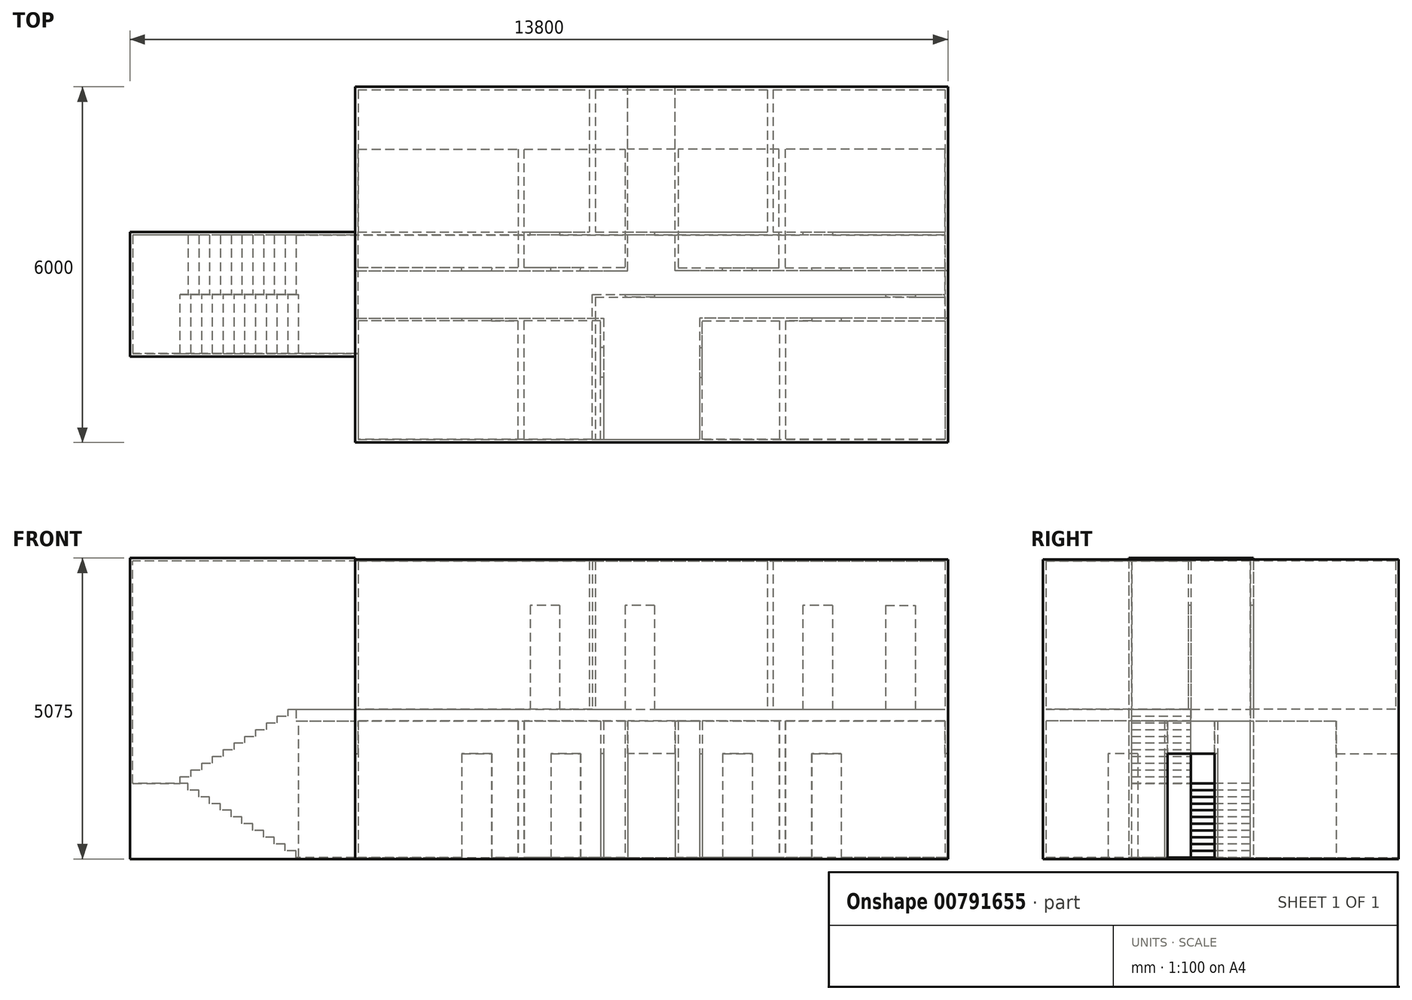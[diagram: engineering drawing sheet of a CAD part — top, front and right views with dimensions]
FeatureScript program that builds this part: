
annotation { "Feature Type Name" : "Feature", "Feature Type Description" : "" }
export const myFeature = defineFeature(function(context is Context, id is Id, definition is map)
    precondition{}
    {
        {
            var Q0;
            Q0=qCreatedBy(makeId("Top.planeOp"),FACE);
            var sketch = newSketch(context, id + "F0", { "sketchPlane" : qUnion([Q0])});
            skLineSegment(sketch, "E0.bottom", {"start": v(0, 0) * mm, "end": v(10000, 0) * mm});
            skLineSegment(sketch, "E0.top", {"start": v(0, 5000) * mm, "end": v(10000, 5000) * mm});
            skLineSegment(sketch, "E0.left", {"start": v(0, 0) * mm, "end": v(0, 5000) * mm});
            skLineSegment(sketch, "E0.right", {"start": v(10000, 0) * mm, "end": v(10000, 5000) * mm});
            skSolve(sketch);
        }
        {
            var Q0;
            Q0=qCreatedBy(makeId("Top.planeOp"),FACE);
            var sketch = newSketch(context, id + "F1", { "sketchPlane" : qUnion([Q0])});
            skLineSegment(sketch, "E1.bottom", {"start": v(0, 0) * mm, "end": v(5000, 0) * mm});
            skLineSegment(sketch, "E1.top", {"start": v(0, 5000) * mm, "end": v(4600, 5000) * mm});
            skLineSegment(sketch, "E1.left", {"start": v(0, 0) * mm, "end": v(0, 2100) * mm});
            skLineSegment(sketch, "E2", {"start": v(0, 2900) * mm, "end": v(1800, 2900) * mm});
            skLineSegment(sketch, "E3", {"start": v(0, 2100) * mm, "end": v(1800, 2100) * mm});
            skLineSegment(sketch, "E4", {"start": v(2800, 2900) * mm, "end": v(2800, 5000) * mm});
            skLineSegment(sketch, "E5", {"start": v(2792.35, 2100) * mm, "end": v(2792.35, 0) * mm});
            skLineSegment(sketch, "E6", {"start": v(2800, 2900) * mm, "end": v(3300, 2900) * mm});
            skLineSegment(sketch, "E7", {"start": v(4600, 2900) * mm, "end": v(4600, 5000) * mm});
            skLineSegment(sketch, "E8", {"start": v(2792.35, 2100) * mm, "end": v(4192.35, 2100) * mm});
            skLineSegment(sketch, "E9", {"start": v(4192.35, 2100) * mm, "end": v(4192.35, 1600) * mm});
            skPoint(sketch, "E10", {"position": v(1800, 2900) * mm});
            skPoint(sketch, "E11", {"position": v(2300, 2900) * mm});
            skPoint(sketch, "E12", {"position": v(1800, 2100) * mm});
            skPoint(sketch, "E13", {"position": v(2300, 2100) * mm});
            skPoint(sketch, "E14", {"position": v(4192.35, 1600) * mm});
            skPoint(sketch, "E15", {"position": v(3300, 2900) * mm});
            skPoint(sketch, "E16", {"position": v(3800, 2900) * mm});
            skPoint(sketch, "E17", {"position": v(4192.35, 1100) * mm});
            skLineSegment(sketch, "E18.trimOffspring", {"start": v(2300, 2900) * mm, "end": v(2800, 2900) * mm});
            skLineSegment(sketch, "E19.trimOffspring", {"start": v(2300, 2100) * mm, "end": v(2792.35, 2100) * mm});
            skLineSegment(sketch, "E20.trimOffspring", {"start": v(3800, 2900) * mm, "end": v(4600, 2900) * mm});
            skLineSegment(sketch, "E21.trimOffspring", {"start": v(4192.35, 1100) * mm, "end": v(4192.35, 0) * mm});
            skLineSegment(sketch, "E22.trimOffspring", {"start": v(0, 2900) * mm, "end": v(0, 5000) * mm});
            skLineSegment(sketch, "E23", {"start": v(1800, 2100) * mm, "end": v(1800, 2050) * mm});
            skLineSegment(sketch, "E24", {"start": v(1800, 2050) * mm, "end": v(50, 2050) * mm});
            skLineSegment(sketch, "E25", {"start": v(50, 2050) * mm, "end": v(50, 50) * mm});
            skLineSegment(sketch, "E26", {"start": v(50, 50) * mm, "end": v(2742.35, 50) * mm});
            skLineSegment(sketch, "E27", {"start": v(2300, 2100) * mm, "end": v(2300, 2050) * mm});
            skLineSegment(sketch, "E28", {"start": v(2300, 2050) * mm, "end": v(2742.35, 2050) * mm});
            skLineSegment(sketch, "E29", {"start": v(2742.35, 2050) * mm, "end": v(2742.35, 50) * mm});
            skLineSegment(sketch, "E30", {"start": v(4192.35, 1600) * mm, "end": v(4142.35, 1600) * mm});
            skLineSegment(sketch, "E31", {"start": v(4142.35, 1600) * mm, "end": v(4142.35, 2050) * mm});
            skLineSegment(sketch, "E32", {"start": v(4142.35, 2050) * mm, "end": v(2842.35, 2050) * mm});
            skLineSegment(sketch, "E33", {"start": v(2842.35, 2050) * mm, "end": v(2842.35, 50) * mm});
            skLineSegment(sketch, "E34", {"start": v(2842.35, 50) * mm, "end": v(4142.35, 50) * mm});
            skLineSegment(sketch, "E35", {"start": v(4192.35, 1100) * mm, "end": v(4142.35, 1100) * mm});
            skLineSegment(sketch, "E36", {"start": v(4142.35, 50) * mm, "end": v(4142.35, 1100) * mm});
            skLineSegment(sketch, "E37", {"start": v(4192.35, 50) * mm, "end": v(5000, 50) * mm});
            skLineSegment(sketch, "E38", {"start": v(5000, 0) * mm, "end": v(5000, 50) * mm});
            skLineSegment(sketch, "E39", {"start": v(1800, 2900) * mm, "end": v(1800, 2950) * mm});
            skLineSegment(sketch, "E40", {"start": v(1800, 2950) * mm, "end": v(50, 2950) * mm});
            skLineSegment(sketch, "E41", {"start": v(50, 2950) * mm, "end": v(50, 4950) * mm});
            skLineSegment(sketch, "E42", {"start": v(50, 4950) * mm, "end": v(2750, 4950) * mm});
            skLineSegment(sketch, "E43", {"start": v(2750, 4950) * mm, "end": v(2750, 2950) * mm});
            skLineSegment(sketch, "E44", {"start": v(2750, 2950) * mm, "end": v(2303.7, 2950) * mm});
            skLineSegment(sketch, "E45", {"start": v(2303.7, 2950) * mm, "end": v(2300, 2900) * mm});
            skLineSegment(sketch, "E46", {"start": v(3300, 2900) * mm, "end": v(3300, 2950) * mm});
            skLineSegment(sketch, "E47", {"start": v(3300, 2950) * mm, "end": v(2850, 2950) * mm});
            skLineSegment(sketch, "E48", {"start": v(2850, 2950) * mm, "end": v(2850, 4950) * mm});
            skLineSegment(sketch, "E49", {"start": v(2850, 4950) * mm, "end": v(4550, 4950) * mm});
            skLineSegment(sketch, "E50", {"start": v(4550, 4950) * mm, "end": v(4550, 2950) * mm});
            skLineSegment(sketch, "E51", {"start": v(4550, 2950) * mm, "end": v(3800.9, 2950) * mm});
            skLineSegment(sketch, "E52", {"start": v(3800, 2900) * mm, "end": v(3800.9, 2950) * mm});
            skSolve(sketch);
        }
        {
            var Q0;
            Q0 = qSketchRegion(id + "F0", true);
            extrude(context, id + "F2", {"entities" : qUnion([Q0]), "oppositeDirection" : true, "depth" : 25 * mm, "offsetDistance" : 25 * mm});
        }
        {
            var Q0;
            Q0 = qSketchRegion(id + "F1", true);
            extrude(context, id + "F3", {"entities" : qUnion([Q0]), "operationType" : NewBodyOperationType.ADD, "depth" : 2500 * mm, "offsetDistance" : 25 * mm});
        }
        {
            var Q0;
            Q0=qCreatedBy(makeId("Top.planeOp"),FACE);
            cPlane(context, id + "F4", {"entities" : qUnion([Q0]), "cplaneType" : CPlaneType.OFFSET, "offset" : 2500 * mm, "width" : 150 * mm, "height" : 150 * mm});
        }
        {
            var Q0;
            Q0=qCreatedBy(id+"F4.planeOp",FACE);
            var sketch = newSketch(context, id + "F5", { "sketchPlane" : qUnion([Q0])});
            skLineSegment(sketch, "E53.bottom", {"start": v(0, 0) * mm, "end": v(10000, 0) * mm});
            skLineSegment(sketch, "E53.top", {"start": v(0, 5000) * mm, "end": v(10000, 5000) * mm});
            skLineSegment(sketch, "E53.left", {"start": v(0, 0) * mm, "end": v(0, 5000) * mm});
            skLineSegment(sketch, "E53.right", {"start": v(10000, 0) * mm, "end": v(10000, 5000) * mm});
            skSolve(sketch);
        }
        {
            var Q0;
            Q0 = qSketchRegion(id + "F5", true);
            extrude(context, id + "F6", {"entities" : qUnion([Q0]), "operationType" : NewBodyOperationType.ADD, "oppositeDirection" : true, "depth" : 200 * mm, "offsetDistance" : 25 * mm});
        }
        {
            var Q0;
            Q0=qCreatedBy(id+"F4.planeOp",FACE);
            var sketch = newSketch(context, id + "F7", { "sketchPlane" : qUnion([Q0])});
            skLineSegment(sketch, "E54.bottom", {"start": v(0, 0) * mm, "end": v(5000, 0) * mm});
            skLineSegment(sketch, "E54.top", {"start": v(0, 5000) * mm, "end": v(4600, 5000) * mm});
            skLineSegment(sketch, "E54.left", {"start": v(0, 0) * mm, "end": v(0, 2100) * mm});
            skLineSegment(sketch, "E55", {"start": v(0, 2900) * mm, "end": v(1800, 2900) * mm});
            skLineSegment(sketch, "E56", {"start": v(0, 2100) * mm, "end": v(1800, 2100) * mm});
            skLineSegment(sketch, "E57", {"start": v(2800, 2900) * mm, "end": v(2800, 5000) * mm});
            skLineSegment(sketch, "E58", {"start": v(2792.35, 2100) * mm, "end": v(2792.35, 0) * mm});
            skLineSegment(sketch, "E59", {"start": v(2800, 2900) * mm, "end": v(3300, 2900) * mm});
            skLineSegment(sketch, "E60", {"start": v(4600, 2900) * mm, "end": v(4600, 5000) * mm});
            skLineSegment(sketch, "E61", {"start": v(2792.35, 2100) * mm, "end": v(4192.35, 2100) * mm});
            skLineSegment(sketch, "E62", {"start": v(4192.35, 2100) * mm, "end": v(4192.35, 1600) * mm});
            skPoint(sketch, "E63", {"position": v(1800, 2900) * mm});
            skPoint(sketch, "E64", {"position": v(2300, 2900) * mm});
            skPoint(sketch, "E65", {"position": v(1800, 2100) * mm});
            skPoint(sketch, "E66", {"position": v(2300, 2100) * mm});
            skPoint(sketch, "E67", {"position": v(4192.35, 1600) * mm});
            skPoint(sketch, "E68", {"position": v(3300, 2900) * mm});
            skPoint(sketch, "E69", {"position": v(3800, 2900) * mm});
            skPoint(sketch, "E70", {"position": v(4192.35, 1100) * mm});
            skLineSegment(sketch, "E71.trimOffspring", {"start": v(2300, 2900) * mm, "end": v(2800, 2900) * mm});
            skLineSegment(sketch, "E72.trimOffspring", {"start": v(2300, 2100) * mm, "end": v(2792.35, 2100) * mm});
            skLineSegment(sketch, "E73.trimOffspring", {"start": v(3800, 2900) * mm, "end": v(4600, 2900) * mm});
            skLineSegment(sketch, "E74.trimOffspring", {"start": v(4192.35, 1100) * mm, "end": v(4192.35, 0) * mm});
            skLineSegment(sketch, "E75.trimOffspring", {"start": v(0, 2900) * mm, "end": v(0, 5000) * mm});
            skLineSegment(sketch, "E76", {"start": v(1800, 2100) * mm, "end": v(1800, 2050) * mm});
            skLineSegment(sketch, "E77", {"start": v(1800, 2050) * mm, "end": v(50, 2050) * mm});
            skLineSegment(sketch, "E78", {"start": v(50, 2050) * mm, "end": v(50, 50) * mm});
            skLineSegment(sketch, "E79", {"start": v(50, 50) * mm, "end": v(2742.35, 50) * mm});
            skLineSegment(sketch, "E80", {"start": v(2300, 2100) * mm, "end": v(2300, 2050) * mm});
            skLineSegment(sketch, "E81", {"start": v(2300, 2050) * mm, "end": v(2742.35, 2050) * mm});
            skLineSegment(sketch, "E82", {"start": v(2742.35, 2050) * mm, "end": v(2742.35, 50) * mm});
            skLineSegment(sketch, "E83", {"start": v(4192.35, 1600) * mm, "end": v(4142.35, 1600) * mm});
            skLineSegment(sketch, "E84", {"start": v(4142.35, 1600) * mm, "end": v(4142.35, 2050) * mm});
            skLineSegment(sketch, "E85", {"start": v(4142.35, 2050) * mm, "end": v(2842.35, 2050) * mm});
            skLineSegment(sketch, "E86", {"start": v(2842.35, 2050) * mm, "end": v(2842.35, 50) * mm});
            skLineSegment(sketch, "E87", {"start": v(2842.35, 50) * mm, "end": v(4142.35, 50) * mm});
            skLineSegment(sketch, "E88", {"start": v(4192.35, 1100) * mm, "end": v(4142.35, 1100) * mm});
            skLineSegment(sketch, "E89", {"start": v(4142.35, 50) * mm, "end": v(4142.35, 1100) * mm});
            skLineSegment(sketch, "E90", {"start": v(4192.35, 50) * mm, "end": v(5000, 50) * mm});
            skLineSegment(sketch, "E91", {"start": v(5000, 0) * mm, "end": v(5000, 50) * mm});
            skLineSegment(sketch, "E92", {"start": v(1800, 2900) * mm, "end": v(1800, 2950) * mm});
            skLineSegment(sketch, "E93", {"start": v(1800, 2950) * mm, "end": v(50, 2950) * mm});
            skLineSegment(sketch, "E94", {"start": v(50, 2950) * mm, "end": v(50, 4950) * mm});
            skLineSegment(sketch, "E95", {"start": v(50, 4950) * mm, "end": v(2750, 4950) * mm});
            skLineSegment(sketch, "E96", {"start": v(2750, 4950) * mm, "end": v(2750, 2950) * mm});
            skLineSegment(sketch, "E97", {"start": v(2750, 2950) * mm, "end": v(2303.7, 2950) * mm});
            skLineSegment(sketch, "E98", {"start": v(2303.7, 2950) * mm, "end": v(2300, 2900) * mm});
            skLineSegment(sketch, "E99", {"start": v(3300, 2900) * mm, "end": v(3300, 2950) * mm});
            skLineSegment(sketch, "E100", {"start": v(3300, 2950) * mm, "end": v(2850, 2950) * mm});
            skLineSegment(sketch, "E101", {"start": v(2850, 2950) * mm, "end": v(2850, 4950) * mm});
            skLineSegment(sketch, "E102", {"start": v(2850, 4950) * mm, "end": v(4550, 4950) * mm});
            skLineSegment(sketch, "E103", {"start": v(4550, 4950) * mm, "end": v(4550, 2950) * mm});
            skLineSegment(sketch, "E104", {"start": v(4550, 2950) * mm, "end": v(3800.9, 2950) * mm});
            skLineSegment(sketch, "E105", {"start": v(3800, 2900) * mm, "end": v(3800.9, 2950) * mm});
            skLineSegment(sketch, "E106", {"start": v(0, 2900) * mm, "end": v(0, 2100) * mm});
            skLineSegment(sketch, "E107", {"start": v(50, 2050) * mm, "end": v(50, 2950) * mm});
            skLineSegment(sketch, "E108", {"start": v(1800, 2050) * mm, "end": v(2300, 2050) * mm});
            skLineSegment(sketch, "E109", {"start": v(2300, 2100) * mm, "end": v(1800, 2100) * mm});
            skLineSegment(sketch, "E110", {"start": v(1800, 2900) * mm, "end": v(2300, 2900) * mm});
            skLineSegment(sketch, "E111", {"start": v(1800, 2950) * mm, "end": v(2303.7, 2950) * mm});
            skLineSegment(sketch, "E112", {"start": v(3300, 2900) * mm, "end": v(3800, 2900) * mm});
            skLineSegment(sketch, "E113", {"start": v(3800.9, 2950) * mm, "end": v(3300, 2950) * mm});
            skLineSegment(sketch, "E114", {"start": v(4192.35, 1600) * mm, "end": v(4192.35, 1100) * mm});
            skLineSegment(sketch, "E115", {"start": v(4142.35, 1100) * mm, "end": v(4142.35, 1600) * mm});
            skLineSegment(sketch, "E116", {"start": v(4600, 5000) * mm, "end": v(5000, 5000) * mm});
            skLineSegment(sketch, "E117", {"start": v(5000, 5000) * mm, "end": v(5000, 4950) * mm});
            skLineSegment(sketch, "E118", {"start": v(5000, 4950) * mm, "end": v(4550, 4950) * mm});
            skSolve(sketch);
        }
        {
            var Q0;
            Q0 = qSketchRegion(id + "F7", true);
            extrude(context, id + "F8", {"entities" : qUnion([Q0]), "operationType" : NewBodyOperationType.ADD, "oppositeDirection" : true, "depth" : 750 * mm, "offsetDistance" : 25 * mm});
        }
        {
            var Q0;
            Q0=makeQuery(id+"F2.opExtrude","SWEPT_BODY",BODY,{"disambiguationData":[OSD([sQuery(id+"F0.wireOp",EDGE,"E0.bottom"),sQuery(id+"F0.wireOp",EDGE,"E0.top"),sQuery(id+"F0.wireOp",EDGE,"E0.left"),sQuery(id+"F0.wireOp",EDGE,"E0.right")])]});
            var Q1;
            Q1=makeQuery(id+"F3.opExtrude","SWEPT_FACE",FACE,{"disambiguationData":[OSD([sQuery(id+"F1.wireOp",EDGE,"E38")])]});
            mirror(context, id + "F9", {"operationType" : NewBodyOperationType.ADD, "entities" : qUnion([Q0]), "mirrorPlane" : qUnion([Q1])});
        }
        {
            var Q0;
            Q0=qCreatedBy(makeId("Front.planeOp"),FACE);
            cPlane(context, id + "F10", {"entities" : qUnion([Q0]), "cplaneType" : CPlaneType.OFFSET, "offset" : 2500 * mm, "oppositeDirection" : true, "width" : 150 * mm, "height" : 150 * mm});
        }
        {
            var Q0;
            Q0=qCreatedBy(id+"F10.planeOp",FACE);
            var sketch = newSketch(context, id + "F11", { "sketchPlane" : qUnion([Q0])});
            skLineSegment(sketch, "E119.bottom", {"start": v(-1000, 0) * mm, "end": v(-3000, 0) * mm});
            skLineSegment(sketch, "E119.right", {"start": v(-3000, 0) * mm, "end": v(-3000, 1250) * mm});
            skLineSegment(sketch, "E120", {"start": v(-1000, 0) * mm, "end": v(-3000, 1250) * mm});
            skLineSegment(sketch, "E121.bottom", {"start": v(-1000, 0) * mm, "end": v(-1181.82, 0) * mm});
            skLineSegment(sketch, "E121.top", {"start": v(-1000, 113.64) * mm, "end": v(-1181.82, 113.64) * mm});
            skLineSegment(sketch, "E121.left", {"start": v(-1000, 0) * mm, "end": v(-1000, 113.64) * mm});
            skLineSegment(sketch, "E121.right", {"start": v(-1181.82, 0) * mm, "end": v(-1181.82, 113.64) * mm});
            skLineSegment(sketch, "E122.bottom", {"start": v(-1181.82, 0) * mm, "end": v(-1363.64, 0) * mm});
            skLineSegment(sketch, "E122.top", {"start": v(-1181.82, 227.27) * mm, "end": v(-1363.64, 227.27) * mm});
            skLineSegment(sketch, "E122.left", {"start": v(-1181.82, 0) * mm, "end": v(-1181.82, 227.27) * mm});
            skLineSegment(sketch, "E122.right", {"start": v(-1363.64, 0) * mm, "end": v(-1363.64, 227.27) * mm});
            skLineSegment(sketch, "E123.bottom", {"start": v(-1363.64, 0) * mm, "end": v(-1545.45, 0) * mm});
            skLineSegment(sketch, "E123.top", {"start": v(-1363.64, 340.9) * mm, "end": v(-1545.45, 340.9) * mm});
            skLineSegment(sketch, "E123.left", {"start": v(-1363.64, 0) * mm, "end": v(-1363.64, 340.9) * mm});
            skLineSegment(sketch, "E123.right", {"start": v(-1545.45, 0) * mm, "end": v(-1545.45, 340.9) * mm});
            skLineSegment(sketch, "E124.bottom", {"start": v(-1545.45, 0) * mm, "end": v(-1727.27, 0) * mm});
            skLineSegment(sketch, "E124.top", {"start": v(-1545.45, 454.55) * mm, "end": v(-1727.27, 454.55) * mm});
            skLineSegment(sketch, "E124.left", {"start": v(-1545.45, 0) * mm, "end": v(-1545.45, 454.55) * mm});
            skLineSegment(sketch, "E124.right", {"start": v(-1727.27, 0) * mm, "end": v(-1727.27, 454.55) * mm});
            skLineSegment(sketch, "E125.bottom", {"start": v(-1727.27, 0) * mm, "end": v(-1909.1, 0) * mm});
            skLineSegment(sketch, "E125.top", {"start": v(-1727.27, 568.18) * mm, "end": v(-1909.1, 568.18) * mm});
            skLineSegment(sketch, "E125.left", {"start": v(-1727.27, 0) * mm, "end": v(-1727.27, 568.18) * mm});
            skLineSegment(sketch, "E125.right", {"start": v(-1909.1, 0) * mm, "end": v(-1909.1, 568.18) * mm});
            skLineSegment(sketch, "E126.bottom", {"start": v(-1909.1, 0) * mm, "end": v(-2090.9, 0) * mm});
            skLineSegment(sketch, "E126.top", {"start": v(-1909.1, 681.81) * mm, "end": v(-2090.9, 681.81) * mm});
            skLineSegment(sketch, "E126.left", {"start": v(-1909.1, 0) * mm, "end": v(-1909.1, 681.81) * mm});
            skLineSegment(sketch, "E126.right", {"start": v(-2090.9, 0) * mm, "end": v(-2090.9, 681.81) * mm});
            skLineSegment(sketch, "E127.bottom", {"start": v(-2090.9, 0) * mm, "end": v(-2272.72, 0) * mm});
            skLineSegment(sketch, "E127.top", {"start": v(-2090.9, 795.45) * mm, "end": v(-2272.72, 795.45) * mm});
            skLineSegment(sketch, "E127.left", {"start": v(-2090.9, 0) * mm, "end": v(-2090.9, 795.45) * mm});
            skLineSegment(sketch, "E127.right", {"start": v(-2272.72, 0) * mm, "end": v(-2272.72, 795.45) * mm});
            skLineSegment(sketch, "E128.bottom", {"start": v(-2272.72, 0) * mm, "end": v(-2454.54, 0) * mm});
            skLineSegment(sketch, "E128.top", {"start": v(-2272.72, 909.09) * mm, "end": v(-2454.54, 909.09) * mm});
            skLineSegment(sketch, "E128.left", {"start": v(-2272.72, 0) * mm, "end": v(-2272.72, 909.09) * mm});
            skLineSegment(sketch, "E128.right", {"start": v(-2454.54, 0) * mm, "end": v(-2454.54, 909.09) * mm});
            skLineSegment(sketch, "E129.bottom", {"start": v(-2454.54, 0) * mm, "end": v(-2636.36, 0) * mm});
            skLineSegment(sketch, "E129.top", {"start": v(-2454.54, 1022.72) * mm, "end": v(-2636.36, 1022.72) * mm});
            skLineSegment(sketch, "E129.left", {"start": v(-2454.54, 0) * mm, "end": v(-2454.54, 1022.72) * mm});
            skLineSegment(sketch, "E129.right", {"start": v(-2636.36, 0) * mm, "end": v(-2636.36, 1022.72) * mm});
            skLineSegment(sketch, "E130.bottom", {"start": v(-2636.36, 0) * mm, "end": v(-2818.17, 0) * mm});
            skLineSegment(sketch, "E130.top", {"start": v(-2636.36, 1136.36) * mm, "end": v(-2818.17, 1136.36) * mm});
            skLineSegment(sketch, "E130.left", {"start": v(-2636.36, 0) * mm, "end": v(-2636.36, 1136.36) * mm});
            skLineSegment(sketch, "E130.right", {"start": v(-2818.17, 0) * mm, "end": v(-2818.17, 1136.36) * mm});
            skLineSegment(sketch, "E131.bottom", {"start": v(-3000, 0) * mm, "end": v(-3750, 0) * mm});
            skLineSegment(sketch, "E131.top", {"start": v(-3000, 1250) * mm, "end": v(-3750, 1250) * mm});
            skLineSegment(sketch, "E131.right", {"start": v(-3750, 0) * mm, "end": v(-3750, 1250) * mm});
            skLineSegment(sketch, "E132.bottom", {"start": v(-2818.17, 0) * mm, "end": v(-3000, 0) * mm});
            skLineSegment(sketch, "E132.top", {"start": v(-2818.17, 1250) * mm, "end": v(-3000, 1250) * mm});
            skLineSegment(sketch, "E132.left", {"start": v(-2818.17, 0) * mm, "end": v(-2818.17, 1250) * mm});
            skSolve(sketch);
        }
        {
            var Q0;
            Q0 = qSketchRegion(id + "F11", true);
            var Q1;
            {var subQ0=makeQuery(id+"F8.boolean.opBoolean","MERGE",FACE,{"derivedFrom":[makeQuery(id+"F6.boolean.opBoolean","MERGE",FACE,{"derivedFrom":[makeQuery(id+"F3.boolean.opBoolean","MERGE",FACE,{"derivedFrom":[makeQuery(id+"F2.opExtrude","SWEPT_FACE",FACE,{"disambiguationData":[OSD([sQuery(id+"F0.wireOp",EDGE,"E0.top")])]}),makeQuery(id+"F3.opExtrude","SWEPT_FACE",FACE,{"disambiguationData":[OSD([sQuery(id+"F1.wireOp",EDGE,"E1.top")])]})]}),makeQuery(id+"F6.opExtrude","SWEPT_FACE",FACE,{"disambiguationData":[OSD([sQuery(id+"F5.wireOp",EDGE,"E53.top")])]})]}),makeQuery(id+"F8.opExtrude","SWEPT_FACE",FACE,{"disambiguationData":[OSD([sQuery(id+"F7.wireOp",EDGE,"E54.top"),sQuery(id+"F7.wireOp",EDGE,"E116")])]})]});Q1=makeQuery(id+"F9.boolean.opBoolean","MERGE",FACE,{"derivedFrom":[subQ0,makeQuery(id+"F9.opPattern","COPY",FACE,{"derivedFrom":subQ0,"instanceName":"1"})]});}
            extrude(context, id + "F12", {"entities" : qUnion([Q0, Q1]), "operationType" : NewBodyOperationType.ADD, "oppositeDirection" : true, "depth" : 1000 * mm, "offsetDistance" : 25 * mm});
        }
        {
            var Q0;
            Q0=qCreatedBy(id+"F10.planeOp",FACE);
            var sketch = newSketch(context, id + "F13", { "sketchPlane" : qUnion([Q0])});
            skLineSegment(sketch, "E133.bottom", {"start": v(-3750, 0) * mm, "end": v(-2950, 0) * mm});
            skLineSegment(sketch, "E133.top", {"start": v(-3750, 1250) * mm, "end": v(-2950, 1250) * mm});
            skLineSegment(sketch, "E133.left", {"start": v(-3750, 0) * mm, "end": v(-3750, 1250) * mm});
            skLineSegment(sketch, "E133.right", {"start": v(-2950, 0) * mm, "end": v(-2950, 1250) * mm});
            skLineSegment(sketch, "E134", {"start": v(-2950, 1250) * mm, "end": v(-950, 1250) * mm});
            skLineSegment(sketch, "E135", {"start": v(-2950, 0) * mm, "end": v(-950, 0) * mm});
            skLineSegment(sketch, "E136", {"start": v(-950, 0) * mm, "end": v(-950, 1250) * mm});
            skLineSegment(sketch, "E137", {"start": v(-950, 1250) * mm, "end": v(-950, 2500) * mm});
            skLineSegment(sketch, "E138", {"start": v(-2950, 1250) * mm, "end": v(-950, 2500) * mm});
            skLineSegment(sketch, "E139.bottom", {"start": v(-2950, 1250) * mm, "end": v(-2768.18, 1250) * mm});
            skLineSegment(sketch, "E139.top", {"start": v(-2950, 1363.64) * mm, "end": v(-2768.18, 1363.64) * mm});
            skLineSegment(sketch, "E139.left", {"start": v(-2950, 1250) * mm, "end": v(-2950, 1363.64) * mm});
            skLineSegment(sketch, "E139.right", {"start": v(-2768.18, 1250) * mm, "end": v(-2768.18, 1363.64) * mm});
            skLineSegment(sketch, "E140.bottom", {"start": v(-2768.18, 1250) * mm, "end": v(-2586.36, 1250) * mm});
            skLineSegment(sketch, "E140.top", {"start": v(-2768.18, 1477.27) * mm, "end": v(-2586.36, 1477.27) * mm});
            skLineSegment(sketch, "E140.left", {"start": v(-2768.18, 1250) * mm, "end": v(-2768.18, 1477.27) * mm});
            skLineSegment(sketch, "E140.right", {"start": v(-2586.36, 1250) * mm, "end": v(-2586.36, 1477.27) * mm});
            skLineSegment(sketch, "E141.bottom", {"start": v(-2586.36, 1250) * mm, "end": v(-2404.55, 1250) * mm});
            skLineSegment(sketch, "E141.top", {"start": v(-2586.36, 1590.9) * mm, "end": v(-2404.55, 1590.9) * mm});
            skLineSegment(sketch, "E141.left", {"start": v(-2586.36, 1250) * mm, "end": v(-2586.36, 1590.9) * mm});
            skLineSegment(sketch, "E141.right", {"start": v(-2404.55, 1250) * mm, "end": v(-2404.55, 1590.9) * mm});
            skLineSegment(sketch, "E142.bottom", {"start": v(-2404.55, 1250) * mm, "end": v(-2222.74, 1250) * mm});
            skLineSegment(sketch, "E142.top", {"start": v(-2404.55, 1704.54) * mm, "end": v(-2222.74, 1704.54) * mm});
            skLineSegment(sketch, "E142.left", {"start": v(-2404.55, 1250) * mm, "end": v(-2404.55, 1704.54) * mm});
            skLineSegment(sketch, "E142.right", {"start": v(-2222.74, 1250) * mm, "end": v(-2222.74, 1704.54) * mm});
            skLineSegment(sketch, "E143.bottom", {"start": v(-2222.74, 1250) * mm, "end": v(-2040.92, 1250) * mm});
            skLineSegment(sketch, "E143.top", {"start": v(-2222.74, 1818.18) * mm, "end": v(-2040.92, 1818.18) * mm});
            skLineSegment(sketch, "E143.left", {"start": v(-2222.74, 1250) * mm, "end": v(-2222.74, 1818.18) * mm});
            skLineSegment(sketch, "E143.right", {"start": v(-2040.92, 1250) * mm, "end": v(-2040.92, 1818.18) * mm});
            skLineSegment(sketch, "E144.bottom", {"start": v(-2040.92, 1250) * mm, "end": v(-1859.1, 1250) * mm});
            skLineSegment(sketch, "E144.top", {"start": v(-2040.92, 1931.81) * mm, "end": v(-1859.1, 1931.81) * mm});
            skLineSegment(sketch, "E144.left", {"start": v(-2040.92, 1250) * mm, "end": v(-2040.92, 1931.81) * mm});
            skLineSegment(sketch, "E144.right", {"start": v(-1859.1, 1250) * mm, "end": v(-1859.1, 1931.81) * mm});
            skLineSegment(sketch, "E145.bottom", {"start": v(-1859.1, 1250) * mm, "end": v(-1677.29, 1250) * mm});
            skLineSegment(sketch, "E145.top", {"start": v(-1859.1, 2045.44) * mm, "end": v(-1677.29, 2045.44) * mm});
            skLineSegment(sketch, "E145.left", {"start": v(-1859.1, 1250) * mm, "end": v(-1859.1, 2045.44) * mm});
            skLineSegment(sketch, "E145.right", {"start": v(-1677.29, 1250) * mm, "end": v(-1677.29, 2045.44) * mm});
            skLineSegment(sketch, "E146.bottom", {"start": v(-1677.29, 1250) * mm, "end": v(-1495.47, 1250) * mm});
            skLineSegment(sketch, "E146.top", {"start": v(-1677.29, 2159.08) * mm, "end": v(-1495.47, 2159.08) * mm});
            skLineSegment(sketch, "E146.left", {"start": v(-1677.29, 1250) * mm, "end": v(-1677.29, 2159.08) * mm});
            skLineSegment(sketch, "E146.right", {"start": v(-1495.47, 1250) * mm, "end": v(-1495.47, 2159.08) * mm});
            skLineSegment(sketch, "E147.bottom", {"start": v(-1495.47, 1250) * mm, "end": v(-1313.65, 1250) * mm});
            skLineSegment(sketch, "E147.top", {"start": v(-1495.47, 2272.72) * mm, "end": v(-1313.65, 2272.72) * mm});
            skLineSegment(sketch, "E147.left", {"start": v(-1495.47, 1250) * mm, "end": v(-1495.47, 2272.72) * mm});
            skLineSegment(sketch, "E147.right", {"start": v(-1313.65, 1250) * mm, "end": v(-1313.65, 2272.72) * mm});
            skLineSegment(sketch, "E148.bottom", {"start": v(-1313.65, 1250) * mm, "end": v(-1131.84, 1250) * mm});
            skLineSegment(sketch, "E148.top", {"start": v(-1313.65, 2386.35) * mm, "end": v(-1131.84, 2386.35) * mm});
            skLineSegment(sketch, "E148.left", {"start": v(-1313.65, 1250) * mm, "end": v(-1313.65, 2386.35) * mm});
            skLineSegment(sketch, "E148.right", {"start": v(-1131.84, 1250) * mm, "end": v(-1131.84, 2386.35) * mm});
            skLineSegment(sketch, "E149.bottom", {"start": v(-1131.84, 1250) * mm, "end": v(-950, 1250) * mm});
            skLineSegment(sketch, "E149.top", {"start": v(-1131.84, 2500) * mm, "end": v(-950, 2500) * mm});
            skLineSegment(sketch, "E149.left", {"start": v(-1131.84, 1250) * mm, "end": v(-1131.84, 2500) * mm});
            skSolve(sketch);
        }
        {
            var Q0;
            Q0 = qSketchRegion(id + "F13", true);
            extrude(context, id + "F14", {"entities" : qUnion([Q0]), "operationType" : NewBodyOperationType.ADD, "depth" : 1000 * mm, "offsetDistance" : 25 * mm});
        }
        {
            var Q0;
            Q0=makeQuery(id+"F8.boolean.opBoolean","MERGE",FACE,{"derivedFrom":[makeQuery(id+"F6.boolean.opBoolean","MERGE",FACE,{"derivedFrom":[makeQuery(id+"F3.boolean.opBoolean","MERGE",FACE,{"derivedFrom":[makeQuery(id+"F2.opExtrude","SWEPT_FACE",FACE,{"disambiguationData":[OSD([sQuery(id+"F0.wireOp",EDGE,"E0.left")])]}),makeQuery(id+"F3.opExtrude","SWEPT_FACE",FACE,{"disambiguationData":[OSD([sQuery(id+"F1.wireOp",EDGE,"E1.left")])]}),makeQuery(id+"F3.opExtrude","SWEPT_FACE",FACE,{"disambiguationData":[OSD([sQuery(id+"F1.wireOp",EDGE,"E22.trimOffspring")])]})]}),makeQuery(id+"F6.opExtrude","SWEPT_FACE",FACE,{"disambiguationData":[OSD([sQuery(id+"F5.wireOp",EDGE,"E53.left")])]})]}),makeQuery(id+"F8.opExtrude","SWEPT_FACE",FACE,{"disambiguationData":[OSD([sQuery(id+"F7.wireOp",EDGE,"E54.left"),sQuery(id+"F7.wireOp",EDGE,"E75.trimOffspring"),sQuery(id+"F7.wireOp",EDGE,"E106")])]})]});
            var sketch = newSketch(context, id + "F15", { "sketchPlane" : qUnion([Q0])});
            skLineSegment(sketch, "E150.top", {"start": v(-1500, 2500) * mm, "end": v(-3500, 2500) * mm});
            skLineSegment(sketch, "E151", {"start": v(-3500, 2500) * mm, "end": v(-3500, 2300) * mm});
            skLineSegment(sketch, "E152", {"start": v(-1500, 2500) * mm, "end": v(-1500, 2300) * mm});
            skLineSegment(sketch, "E153", {"start": v(-1500, 2300) * mm, "end": v(-3500, 2300) * mm});
            skSolve(sketch);
        }
        {
            var Q0;
            Q0 = qSketchRegion(id + "F15", true);
            extrude(context, id + "F16", {"entities" : qUnion([Q0]), "operationType" : NewBodyOperationType.ADD, "depth" : 1000 * mm, "offsetDistance" : 25 * mm});
        }
        {
            var Q0;
            Q0=makeQuery(id+"F14.boolean.opBoolean","MERGE",FACE,{"derivedFrom":[makeQuery(id+"F12.opExtrude","SWEPT_FACE",FACE,{"disambiguationData":[OSD([sQuery(id+"F11.wireOp",EDGE,"E131.right")])]}),makeQuery(id+"F14.opExtrude","SWEPT_FACE",FACE,{"disambiguationData":[OSD([sQuery(id+"F13.wireOp",EDGE,"E133.left")])]})]});
            var sketch = newSketch(context, id + "F17", { "sketchPlane" : qUnion([Q0])});
            skLineSegment(sketch, "E154.bottom", {"start": v(-3500, 0) * mm, "end": v(-1500, 0) * mm});
            skLineSegment(sketch, "E154.top", {"start": v(-3500, 5000) * mm, "end": v(-1500, 5000) * mm});
            skLineSegment(sketch, "E154.left", {"start": v(-3500, 0) * mm, "end": v(-3500, 5000) * mm});
            skLineSegment(sketch, "E154.right", {"start": v(-1500, 0) * mm, "end": v(-1500, 5000) * mm});
            skLineSegment(sketch, "E155.bottom", {"start": v(-3550, 5050) * mm, "end": v(-1450, 5050) * mm});
            skLineSegment(sketch, "E155.top", {"start": v(-3550, -25) * mm, "end": v(-1450, -25) * mm});
            skLineSegment(sketch, "E155.left", {"start": v(-3550, 5050) * mm, "end": v(-3550, -25) * mm});
            skLineSegment(sketch, "E155.right", {"start": v(-1450, 5050) * mm, "end": v(-1450, -25) * mm});
            skSolve(sketch);
        }
        {
            var Q0;
            Q0 = qSketchRegion(id + "F17", true);
            extrude(context, id + "F18", {"entities" : qUnion([Q0]), "operationType" : NewBodyOperationType.ADD, "oppositeDirection" : true, "depth" : 3750 * mm, "offsetDistance" : 25 * mm});
        }
        {
            var Q0;
            Q0=makeQuery(id+"F18.boolean.opBoolean","MERGE",FACE,{"derivedFrom":[makeQuery(id+"F14.boolean.opBoolean","MERGE",FACE,{"derivedFrom":[makeQuery(id+"F12.opExtrude","SWEPT_FACE",FACE,{"disambiguationData":[OSD([sQuery(id+"F11.wireOp",EDGE,"E131.right")])]}),makeQuery(id+"F14.opExtrude","SWEPT_FACE",FACE,{"disambiguationData":[OSD([sQuery(id+"F13.wireOp",EDGE,"E133.left")])]})]}),makeQuery(id+"F18.opExtrude","CAP_FACE",FACE,{"disambiguationData":[OSD([sQuery(id+"F17.wireOp",EDGE,"E154.bottom"),sQuery(id+"F17.wireOp",EDGE,"E154.top"),sQuery(id+"F17.wireOp",EDGE,"E154.left"),sQuery(id+"F17.wireOp",EDGE,"E154.right"),sQuery(id+"F17.wireOp",EDGE,"E155.bottom"),sQuery(id+"F17.wireOp",EDGE,"E155.top"),sQuery(id+"F17.wireOp",EDGE,"E155.left"),sQuery(id+"F17.wireOp",EDGE,"E155.right")])],"isStart":true})]});
            var sketch = newSketch(context, id + "F19", { "sketchPlane" : qUnion([Q0])});
            skLineSegment(sketch, "E156.bottom", {"start": v(-3550, -25) * mm, "end": v(-1450, -25) * mm});
            skLineSegment(sketch, "E156.top", {"start": v(-3550, 5050) * mm, "end": v(-1450, 5050) * mm});
            skLineSegment(sketch, "E156.left", {"start": v(-3550, -25) * mm, "end": v(-3550, 5050) * mm});
            skLineSegment(sketch, "E156.right", {"start": v(-1450, -25) * mm, "end": v(-1450, 5050) * mm});
            skSolve(sketch);
        }
        {
            var Q0;
            Q0 = qSketchRegion(id + "F19", true);
            extrude(context, id + "F20", {"entities" : qUnion([Q0]), "operationType" : NewBodyOperationType.ADD, "depth" : 50 * mm, "offsetDistance" : 25 * mm});
        }
        {
            var Q0;
            {var subQ0=sQuery(id+"F5.wireOp",EDGE,"E53.top");var subQ1=sQuery(id+"F1.wireOp",EDGE,"E1.top");Q0=makeQuery(id+"F16.boolean.opBoolean","MERGE",FACE,{"derivedFrom":[makeQuery(id+"F12.boolean.opBoolean","MERGE",FACE,{"derivedFrom":[makeQuery(id+"F6.boolean.opBoolean","MERGE",FACE,{"derivedFrom":[makeQuery(id+"F3.opExtrude","CAP_FACE",FACE,{"disambiguationData":[OSD([sQuery(id+"F1.wireOp",EDGE,"E1.bottom"),sQuery(id+"F1.wireOp",EDGE,"E1.left"),sQuery(id+"F1.wireOp",EDGE,"E3"),sQuery(id+"F1.wireOp",EDGE,"E8"),sQuery(id+"F1.wireOp",EDGE,"E9"),sQuery(id+"F1.wireOp",EDGE,"E19.trimOffspring"),sQuery(id+"F1.wireOp",EDGE,"E21.trimOffspring"),sQuery(id+"F1.wireOp",EDGE,"E23"),sQuery(id+"F1.wireOp",EDGE,"E24"),sQuery(id+"F1.wireOp",EDGE,"E25"),sQuery(id+"F1.wireOp",EDGE,"E26"),sQuery(id+"F1.wireOp",EDGE,"E27"),sQuery(id+"F1.wireOp",EDGE,"E28"),sQuery(id+"F1.wireOp",EDGE,"E29"),sQuery(id+"F1.wireOp",EDGE,"E30"),sQuery(id+"F1.wireOp",EDGE,"E31"),sQuery(id+"F1.wireOp",EDGE,"E32"),sQuery(id+"F1.wireOp",EDGE,"E33"),sQuery(id+"F1.wireOp",EDGE,"E34"),sQuery(id+"F1.wireOp",EDGE,"E35"),sQuery(id+"F1.wireOp",EDGE,"E36"),sQuery(id+"F1.wireOp",EDGE,"E37"),sQuery(id+"F1.wireOp",EDGE,"E38")])],"isStart":false}),makeQuery(id+"F3.opExtrude","CAP_FACE",FACE,{"disambiguationData":[OSD([subQ1,sQuery(id+"F1.wireOp",EDGE,"E2"),sQuery(id+"F1.wireOp",EDGE,"E6"),sQuery(id+"F1.wireOp",EDGE,"E7"),sQuery(id+"F1.wireOp",EDGE,"E18.trimOffspring"),sQuery(id+"F1.wireOp",EDGE,"E20.trimOffspring"),sQuery(id+"F1.wireOp",EDGE,"E22.trimOffspring"),sQuery(id+"F1.wireOp",EDGE,"E39"),sQuery(id+"F1.wireOp",EDGE,"E40"),sQuery(id+"F1.wireOp",EDGE,"E41"),sQuery(id+"F1.wireOp",EDGE,"E42"),sQuery(id+"F1.wireOp",EDGE,"E43"),sQuery(id+"F1.wireOp",EDGE,"E44"),sQuery(id+"F1.wireOp",EDGE,"E45"),sQuery(id+"F1.wireOp",EDGE,"E46"),sQuery(id+"F1.wireOp",EDGE,"E47"),sQuery(id+"F1.wireOp",EDGE,"E48"),sQuery(id+"F1.wireOp",EDGE,"E49"),sQuery(id+"F1.wireOp",EDGE,"E50"),sQuery(id+"F1.wireOp",EDGE,"E51"),sQuery(id+"F1.wireOp",EDGE,"E52")])],"isStart":false}),makeQuery(id+"F6.opExtrude","CAP_FACE",FACE,{"disambiguationData":[OSD([sQuery(id+"F5.wireOp",EDGE,"E53.bottom"),subQ0,sQuery(id+"F5.wireOp",EDGE,"E53.left"),sQuery(id+"F5.wireOp",EDGE,"E53.right")])],"isStart":true})]}),makeQuery(id+"F12.opExtrude","SWEPT_FACE",FACE,{"disambiguationData":[OSD([subQ1,subQ0])]})]}),makeQuery(id+"F14.opExtrude","SWEPT_FACE",FACE,{"disambiguationData":[OSD([sQuery(id+"F13.wireOp",EDGE,"E149.top")])]}),makeQuery(id+"F16.opExtrude","SWEPT_FACE",FACE,{"disambiguationData":[OSD([sQuery(id+"F15.wireOp",EDGE,"E150.top")])]})]});}
            var sketch = newSketch(context, id + "F21", { "sketchPlane" : qUnion([Q0])});
            skLineSegment(sketch, "E157.bottom", {"start": v(0, 6000) * mm, "end": v(10000, 6000) * mm});
            skLineSegment(sketch, "E157.top", {"start": v(0, 0) * mm, "end": v(10000, 0) * mm});
            skLineSegment(sketch, "E157.right", {"start": v(10000, 6000) * mm, "end": v(10000, 0) * mm});
            skPoint(sketch, "E158", {"position": v(0, 3550) * mm});
            skPoint(sketch, "E159", {"position": v(0, 1450) * mm});
            skLineSegment(sketch, "E160.trimOffspring", {"start": v(0, 1450) * mm, "end": v(0, 0) * mm});
            skLineSegment(sketch, "E161", {"start": v(4000, 3500) * mm, "end": v(4000, 6000) * mm});
            skLineSegment(sketch, "E162", {"start": v(4000, 0) * mm, "end": v(4000, 2500) * mm});
            skLineSegment(sketch, "E163", {"start": v(4000, 2500) * mm, "end": v(4550, 2500) * mm});
            skLineSegment(sketch, "E164", {"start": v(4000, 3500) * mm, "end": v(4550, 3500) * mm});
            skLineSegment(sketch, "E165", {"start": v(7000, 3500) * mm, "end": v(7000, 6000) * mm});
            skLineSegment(sketch, "E166", {"start": v(7000, 3500) * mm, "end": v(7550, 3500) * mm});
            skLineSegment(sketch, "E167.bottom", {"start": v(50, 5950) * mm, "end": v(3950, 5950) * mm});
            skLineSegment(sketch, "E167.top", {"start": v(50, 3550) * mm, "end": v(2950, 3550) * mm});
            skLineSegment(sketch, "E167.left", {"start": v(50, 5950) * mm, "end": v(50, 3550) * mm});
            skLineSegment(sketch, "E167.right", {"start": v(3950, 5950) * mm, "end": v(3950, 3550) * mm});
            skLineSegment(sketch, "E168.bottom", {"start": v(4050, 5950) * mm, "end": v(6950, 5950) * mm});
            skLineSegment(sketch, "E168.top", {"start": v(4050, 3550) * mm, "end": v(4550, 3550) * mm});
            skLineSegment(sketch, "E168.left", {"start": v(4050, 5950) * mm, "end": v(4050, 3550) * mm});
            skLineSegment(sketch, "E168.right", {"start": v(6950, 5950) * mm, "end": v(6950, 3550) * mm});
            skLineSegment(sketch, "E169.bottom", {"start": v(7050, 5950) * mm, "end": v(9950, 5950) * mm});
            skLineSegment(sketch, "E169.top", {"start": v(7050, 3550) * mm, "end": v(7550, 3550) * mm});
            skLineSegment(sketch, "E169.left", {"start": v(7050, 5950) * mm, "end": v(7050, 3550) * mm});
            skLineSegment(sketch, "E169.right", {"start": v(9950, 5950) * mm, "end": v(9950, 3550) * mm});
            skLineSegment(sketch, "E170", {"start": v(9950, 3500) * mm, "end": v(9950, 2500) * mm});
            skLineSegment(sketch, "E171.bottom", {"start": v(4050, 2450) * mm, "end": v(4550, 2450) * mm});
            skLineSegment(sketch, "E171.top", {"start": v(4050, 50) * mm, "end": v(9950, 50) * mm});
            skLineSegment(sketch, "E171.left", {"start": v(4050, 2450) * mm, "end": v(4050, 50) * mm});
            skLineSegment(sketch, "E171.right", {"start": v(9950, 2450) * mm, "end": v(9950, 50) * mm});
            skLineSegment(sketch, "E172", {"start": v(0, 1450) * mm, "end": v(0, 1500) * mm});
            skLineSegment(sketch, "E173", {"start": v(0, 1500) * mm, "end": v(50, 1500) * mm});
            skLineSegment(sketch, "E174", {"start": v(50, 1500) * mm, "end": v(50, 0) * mm});
            skLineSegment(sketch, "E175", {"start": v(4000, 50) * mm, "end": v(50, 50) * mm});
            skPoint(sketch, "E176", {"position": v(3450, 3550) * mm});
            skPoint(sketch, "E177", {"position": v(2950, 3550) * mm});
            skPoint(sketch, "E178", {"position": v(3450, 3500) * mm});
            skLineSegment(sketch, "E179", {"start": v(3450, 3550) * mm, "end": v(3450, 3500) * mm});
            skLineSegment(sketch, "E180.trimOffspring", {"start": v(3450, 3550) * mm, "end": v(3950, 3550) * mm});
            skLineSegment(sketch, "E181.trimOffspring", {"start": v(3450, 3500) * mm, "end": v(4000, 3500) * mm});
            skPoint(sketch, "E182", {"position": v(4550, 3550) * mm});
            skPoint(sketch, "E183", {"position": v(5050, 3550) * mm});
            skPoint(sketch, "E184", {"position": v(4550, 3500) * mm});
            skPoint(sketch, "E185", {"position": v(5050, 3500) * mm});
            skLineSegment(sketch, "E186", {"start": v(4550, 3550) * mm, "end": v(4550, 3500) * mm});
            skLineSegment(sketch, "E187", {"start": v(5050, 3550) * mm, "end": v(5050, 3500) * mm});
            skLineSegment(sketch, "E188.trimOffspring", {"start": v(5050, 3550) * mm, "end": v(6950, 3550) * mm});
            skLineSegment(sketch, "E189.trimOffspring", {"start": v(5050, 3500) * mm, "end": v(7000, 3500) * mm});
            skPoint(sketch, "E190", {"position": v(7550, 3550) * mm});
            skPoint(sketch, "E191", {"position": v(4550, 2500) * mm});
            skPoint(sketch, "E192", {"position": v(4550, 2450) * mm});
            skPoint(sketch, "E193", {"position": v(5050, 2500) * mm});
            skPoint(sketch, "E194", {"position": v(5050, 2450) * mm});
            skPoint(sketch, "E195", {"position": v(8050, 3550) * mm});
            skPoint(sketch, "E196", {"position": v(7550, 3500) * mm});
            skPoint(sketch, "E197", {"position": v(8050, 3500) * mm});
            skPoint(sketch, "E198", {"position": v(9450, 2500) * mm});
            skPoint(sketch, "E199", {"position": v(9450, 2450) * mm});
            skPoint(sketch, "E200", {"position": v(8950, 2500) * mm});
            skPoint(sketch, "E201", {"position": v(8950, 2450) * mm});
            skLineSegment(sketch, "E202", {"start": v(8950, 2500) * mm, "end": v(8950, 2450) * mm});
            skLineSegment(sketch, "E203", {"start": v(9450, 2500) * mm, "end": v(9450, 2450) * mm});
            skLineSegment(sketch, "E204", {"start": v(8050, 3550) * mm, "end": v(8050, 3500) * mm});
            skLineSegment(sketch, "E205", {"start": v(7550, 3550) * mm, "end": v(7550, 3500) * mm});
            skLineSegment(sketch, "E206", {"start": v(4550, 2500) * mm, "end": v(4550, 2450) * mm});
            skLineSegment(sketch, "E207", {"start": v(5050, 2500) * mm, "end": v(5050, 2450) * mm});
            skLineSegment(sketch, "E208.trimOffspring", {"start": v(5050, 2500) * mm, "end": v(8950, 2500) * mm});
            skLineSegment(sketch, "E209.trimOffspring", {"start": v(5050, 2450) * mm, "end": v(8950, 2450) * mm});
            skLineSegment(sketch, "E210.trimOffspring", {"start": v(8050, 3550) * mm, "end": v(9950, 3550) * mm});
            skLineSegment(sketch, "E211.trimOffspring", {"start": v(8050, 3500) * mm, "end": v(10000, 3500) * mm});
            skLineSegment(sketch, "E212.trimOffspring", {"start": v(9450, 2500) * mm, "end": v(10000, 2500) * mm});
            skLineSegment(sketch, "E213.trimOffspring", {"start": v(9450, 2450) * mm, "end": v(9950, 2450) * mm});
            skLineSegment(sketch, "E214", {"start": v(0, 6000) * mm, "end": v(0, 3550) * mm});
            skLineSegment(sketch, "E215", {"start": v(0, 3500) * mm, "end": v(0, 3550) * mm});
            skLineSegment(sketch, "E216", {"start": v(0, 3500) * mm, "end": v(2950, 3500) * mm});
            skLineSegment(sketch, "E217", {"start": v(2950, 3500) * mm, "end": v(2950, 3550) * mm});
            skSolve(sketch);
        }
        {
            var Q0;
            Q0 = qSketchRegion(id + "F21", true);
            extrude(context, id + "F22", {"entities" : qUnion([Q0]), "operationType" : NewBodyOperationType.ADD, "depth" : 2500 * mm, "offsetDistance" : 25 * mm});
        }
        {
            var Q0;
            Q0=makeQuery(id+"F22.opExtrude","CAP_FACE",FACE,{"disambiguationData":[OSD([sQuery(id+"F21.wireOp",EDGE,"E157.bottom"),sQuery(id+"F21.wireOp",EDGE,"E157.top"),sQuery(id+"F21.wireOp",EDGE,"E157.right"),sQuery(id+"F21.wireOp",EDGE,"E160.trimOffspring"),sQuery(id+"F21.wireOp",EDGE,"E162"),sQuery(id+"F21.wireOp",EDGE,"E163"),sQuery(id+"F21.wireOp",EDGE,"E164"),sQuery(id+"F21.wireOp",EDGE,"E166"),sQuery(id+"F21.wireOp",EDGE,"E167.bottom"),sQuery(id+"F21.wireOp",EDGE,"E167.top"),sQuery(id+"F21.wireOp",EDGE,"E167.left"),sQuery(id+"F21.wireOp",EDGE,"E167.right"),sQuery(id+"F21.wireOp",EDGE,"E168.bottom"),sQuery(id+"F21.wireOp",EDGE,"E168.top"),sQuery(id+"F21.wireOp",EDGE,"E168.left"),sQuery(id+"F21.wireOp",EDGE,"E168.right"),sQuery(id+"F21.wireOp",EDGE,"E169.bottom"),sQuery(id+"F21.wireOp",EDGE,"E169.top"),sQuery(id+"F21.wireOp",EDGE,"E169.left"),sQuery(id+"F21.wireOp",EDGE,"E169.right"),sQuery(id+"F21.wireOp",EDGE,"E170"),sQuery(id+"F21.wireOp",EDGE,"E171.bottom"),sQuery(id+"F21.wireOp",EDGE,"E171.top"),sQuery(id+"F21.wireOp",EDGE,"E171.left"),sQuery(id+"F21.wireOp",EDGE,"E171.right"),sQuery(id+"F21.wireOp",EDGE,"E172"),sQuery(id+"F21.wireOp",EDGE,"E173"),sQuery(id+"F21.wireOp",EDGE,"E174"),sQuery(id+"F21.wireOp",EDGE,"E175"),sQuery(id+"F21.wireOp",EDGE,"E179"),sQuery(id+"F21.wireOp",EDGE,"E180.trimOffspring"),sQuery(id+"F21.wireOp",EDGE,"E181.trimOffspring"),sQuery(id+"F21.wireOp",EDGE,"E186"),sQuery(id+"F21.wireOp",EDGE,"E187"),sQuery(id+"F21.wireOp",EDGE,"E188.trimOffspring"),sQuery(id+"F21.wireOp",EDGE,"E189.trimOffspring"),sQuery(id+"F21.wireOp",EDGE,"E203"),sQuery(id+"F21.wireOp",EDGE,"E204"),sQuery(id+"F21.wireOp",EDGE,"E205"),sQuery(id+"F21.wireOp",EDGE,"E206"),sQuery(id+"F21.wireOp",EDGE,"E210.trimOffspring"),sQuery(id+"F21.wireOp",EDGE,"E211.trimOffspring"),sQuery(id+"F21.wireOp",EDGE,"E212.trimOffspring"),sQuery(id+"F21.wireOp",EDGE,"E213.trimOffspring"),sQuery(id+"F21.wireOp",EDGE,"E214"),sQuery(id+"F21.wireOp",EDGE,"E215"),sQuery(id+"F21.wireOp",EDGE,"E216"),sQuery(id+"F21.wireOp",EDGE,"E217")])],"isStart":false});
            var sketch = newSketch(context, id + "F23", { "sketchPlane" : qUnion([Q0])});
            skLineSegment(sketch, "E218.bottom", {"start": v(0, 6000) * mm, "end": v(10000, 6000) * mm});
            skLineSegment(sketch, "E218.top", {"start": v(0, 0) * mm, "end": v(10000, 0) * mm});
            skLineSegment(sketch, "E218.right", {"start": v(10000, 6000) * mm, "end": v(10000, 0) * mm});
            skPoint(sketch, "E219", {"position": v(0, 3550) * mm});
            skPoint(sketch, "E220", {"position": v(0, 1450) * mm});
            skLineSegment(sketch, "E221.trimOffspring", {"start": v(0, 1450) * mm, "end": v(0, 0) * mm});
            skLineSegment(sketch, "E222", {"start": v(4000, 3500) * mm, "end": v(4000, 6000) * mm});
            skLineSegment(sketch, "E223", {"start": v(4000, 0) * mm, "end": v(4000, 2500) * mm});
            skLineSegment(sketch, "E224", {"start": v(4000, 2500) * mm, "end": v(4550, 2500) * mm});
            skLineSegment(sketch, "E225", {"start": v(4000, 3500) * mm, "end": v(4550, 3500) * mm});
            skLineSegment(sketch, "E226", {"start": v(7000, 3500) * mm, "end": v(7000, 6000) * mm});
            skLineSegment(sketch, "E227", {"start": v(7000, 3500) * mm, "end": v(7550, 3500) * mm});
            skLineSegment(sketch, "E228.bottom", {"start": v(50, 5950) * mm, "end": v(3950, 5950) * mm});
            skLineSegment(sketch, "E228.top", {"start": v(50, 3550) * mm, "end": v(2950, 3550) * mm});
            skLineSegment(sketch, "E228.left", {"start": v(50, 5950) * mm, "end": v(50, 3550) * mm});
            skLineSegment(sketch, "E228.right", {"start": v(3950, 5950) * mm, "end": v(3950, 3550) * mm});
            skLineSegment(sketch, "E229.bottom", {"start": v(4050, 5950) * mm, "end": v(6950, 5950) * mm});
            skLineSegment(sketch, "E229.top", {"start": v(4050, 3550) * mm, "end": v(4550, 3550) * mm});
            skLineSegment(sketch, "E229.left", {"start": v(4050, 5950) * mm, "end": v(4050, 3550) * mm});
            skLineSegment(sketch, "E229.right", {"start": v(6950, 5950) * mm, "end": v(6950, 3550) * mm});
            skLineSegment(sketch, "E230.bottom", {"start": v(7050, 5950) * mm, "end": v(9950, 5950) * mm});
            skLineSegment(sketch, "E230.top", {"start": v(7050, 3550) * mm, "end": v(7550, 3550) * mm});
            skLineSegment(sketch, "E230.left", {"start": v(7050, 5950) * mm, "end": v(7050, 3550) * mm});
            skLineSegment(sketch, "E230.right", {"start": v(9950, 5950) * mm, "end": v(9950, 3550) * mm});
            skLineSegment(sketch, "E231", {"start": v(9950, 3500) * mm, "end": v(9950, 2500) * mm});
            skLineSegment(sketch, "E232.bottom", {"start": v(4050, 2450) * mm, "end": v(4550, 2450) * mm});
            skLineSegment(sketch, "E232.top", {"start": v(4050, 50) * mm, "end": v(9950, 50) * mm});
            skLineSegment(sketch, "E232.left", {"start": v(4050, 2450) * mm, "end": v(4050, 50) * mm});
            skLineSegment(sketch, "E232.right", {"start": v(9950, 2450) * mm, "end": v(9950, 50) * mm});
            skLineSegment(sketch, "E233", {"start": v(0, 1450) * mm, "end": v(0, 1500) * mm});
            skLineSegment(sketch, "E234", {"start": v(0, 1500) * mm, "end": v(50, 1500) * mm});
            skLineSegment(sketch, "E235", {"start": v(50, 1500) * mm, "end": v(50, 0) * mm});
            skLineSegment(sketch, "E236", {"start": v(4000, 50) * mm, "end": v(50, 50) * mm});
            skPoint(sketch, "E237", {"position": v(3450, 3550) * mm});
            skPoint(sketch, "E238", {"position": v(2950, 3550) * mm});
            skPoint(sketch, "E239", {"position": v(3450, 3500) * mm});
            skLineSegment(sketch, "E240", {"start": v(3450, 3550) * mm, "end": v(3450, 3500) * mm});
            skLineSegment(sketch, "E241.trimOffspring", {"start": v(3450, 3550) * mm, "end": v(3950, 3550) * mm});
            skLineSegment(sketch, "E242.trimOffspring", {"start": v(3450, 3500) * mm, "end": v(4000, 3500) * mm});
            skPoint(sketch, "E243", {"position": v(4550, 3550) * mm});
            skPoint(sketch, "E244", {"position": v(5050, 3550) * mm});
            skPoint(sketch, "E245", {"position": v(4550, 3500) * mm});
            skPoint(sketch, "E246", {"position": v(5050, 3500) * mm});
            skLineSegment(sketch, "E247", {"start": v(4550, 3550) * mm, "end": v(4550, 3500) * mm});
            skLineSegment(sketch, "E248", {"start": v(5050, 3550) * mm, "end": v(5050, 3500) * mm});
            skLineSegment(sketch, "E249.trimOffspring", {"start": v(5050, 3550) * mm, "end": v(6950, 3550) * mm});
            skLineSegment(sketch, "E250.trimOffspring", {"start": v(5050, 3500) * mm, "end": v(7000, 3500) * mm});
            skPoint(sketch, "E251", {"position": v(7550, 3550) * mm});
            skPoint(sketch, "E252", {"position": v(4550, 2500) * mm});
            skPoint(sketch, "E253", {"position": v(4550, 2450) * mm});
            skPoint(sketch, "E254", {"position": v(5050, 2500) * mm});
            skPoint(sketch, "E255", {"position": v(5050, 2450) * mm});
            skPoint(sketch, "E256", {"position": v(8050, 3550) * mm});
            skPoint(sketch, "E257", {"position": v(7550, 3500) * mm});
            skPoint(sketch, "E258", {"position": v(8050, 3500) * mm});
            skPoint(sketch, "E259", {"position": v(9450, 2500) * mm});
            skPoint(sketch, "E260", {"position": v(9450, 2450) * mm});
            skPoint(sketch, "E261", {"position": v(8950, 2500) * mm});
            skPoint(sketch, "E262", {"position": v(8950, 2450) * mm});
            skLineSegment(sketch, "E263", {"start": v(8950, 2500) * mm, "end": v(8950, 2450) * mm});
            skLineSegment(sketch, "E264", {"start": v(9450, 2500) * mm, "end": v(9450, 2450) * mm});
            skLineSegment(sketch, "E265", {"start": v(8050, 3550) * mm, "end": v(8050, 3500) * mm});
            skLineSegment(sketch, "E266", {"start": v(7550, 3550) * mm, "end": v(7550, 3500) * mm});
            skLineSegment(sketch, "E267", {"start": v(4550, 2500) * mm, "end": v(4550, 2450) * mm});
            skLineSegment(sketch, "E268", {"start": v(5050, 2500) * mm, "end": v(5050, 2450) * mm});
            skLineSegment(sketch, "E269.trimOffspring", {"start": v(5050, 2500) * mm, "end": v(8950, 2500) * mm});
            skLineSegment(sketch, "E270.trimOffspring", {"start": v(5050, 2450) * mm, "end": v(8950, 2450) * mm});
            skLineSegment(sketch, "E271.trimOffspring", {"start": v(8050, 3550) * mm, "end": v(9950, 3550) * mm});
            skLineSegment(sketch, "E272.trimOffspring", {"start": v(8050, 3500) * mm, "end": v(10000, 3500) * mm});
            skLineSegment(sketch, "E273.trimOffspring", {"start": v(9450, 2500) * mm, "end": v(10000, 2500) * mm});
            skLineSegment(sketch, "E274.trimOffspring", {"start": v(9450, 2450) * mm, "end": v(9950, 2450) * mm});
            skLineSegment(sketch, "E275", {"start": v(0, 6000) * mm, "end": v(0, 3550) * mm});
            skLineSegment(sketch, "E276", {"start": v(0, 3500) * mm, "end": v(0, 3550) * mm});
            skLineSegment(sketch, "E277", {"start": v(0, 3500) * mm, "end": v(2950, 3500) * mm});
            skLineSegment(sketch, "E278", {"start": v(2950, 3500) * mm, "end": v(2950, 3550) * mm});
            skLineSegment(sketch, "E279", {"start": v(2950, 3550) * mm, "end": v(3450, 3550) * mm});
            skLineSegment(sketch, "E280", {"start": v(3450, 3500) * mm, "end": v(2950, 3500) * mm});
            skLineSegment(sketch, "E281", {"start": v(4550, 3550) * mm, "end": v(5050, 3550) * mm});
            skLineSegment(sketch, "E282", {"start": v(5050, 3500) * mm, "end": v(4550, 3500) * mm});
            skLineSegment(sketch, "E283", {"start": v(4550, 2500) * mm, "end": v(5050, 2500) * mm});
            skLineSegment(sketch, "E284", {"start": v(4550, 2450) * mm, "end": v(5050, 2450) * mm});
            skLineSegment(sketch, "E285", {"start": v(7550, 3550) * mm, "end": v(8050, 3550) * mm});
            skLineSegment(sketch, "E286", {"start": v(8050, 3500) * mm, "end": v(7550, 3500) * mm});
            skLineSegment(sketch, "E287", {"start": v(8950, 2500) * mm, "end": v(9450, 2500) * mm});
            skLineSegment(sketch, "E288", {"start": v(9450, 2450) * mm, "end": v(8950, 2450) * mm});
            skSolve(sketch);
        }
        {
            var Q0;
            Q0 = qSketchRegion(id + "F23", true);
            extrude(context, id + "F24", {"entities" : qUnion([Q0]), "operationType" : NewBodyOperationType.ADD, "oppositeDirection" : true, "depth" : 750 * mm, "offsetDistance" : 25 * mm});
        }
        {
            var Q0;
            Q0=makeQuery(id+"F24.boolean.opBoolean","MERGE",FACE,{"derivedFrom":[makeQuery(id+"F22.opExtrude","CAP_FACE",FACE,{"disambiguationData":[OSD([sQuery(id+"F21.wireOp",EDGE,"E157.bottom"),sQuery(id+"F21.wireOp",EDGE,"E157.top"),sQuery(id+"F21.wireOp",EDGE,"E157.right"),sQuery(id+"F21.wireOp",EDGE,"E160.trimOffspring"),sQuery(id+"F21.wireOp",EDGE,"E162"),sQuery(id+"F21.wireOp",EDGE,"E163"),sQuery(id+"F21.wireOp",EDGE,"E164"),sQuery(id+"F21.wireOp",EDGE,"E166"),sQuery(id+"F21.wireOp",EDGE,"E167.bottom"),sQuery(id+"F21.wireOp",EDGE,"E167.top"),sQuery(id+"F21.wireOp",EDGE,"E167.left"),sQuery(id+"F21.wireOp",EDGE,"E167.right"),sQuery(id+"F21.wireOp",EDGE,"E168.bottom"),sQuery(id+"F21.wireOp",EDGE,"E168.top"),sQuery(id+"F21.wireOp",EDGE,"E168.left"),sQuery(id+"F21.wireOp",EDGE,"E168.right"),sQuery(id+"F21.wireOp",EDGE,"E169.bottom"),sQuery(id+"F21.wireOp",EDGE,"E169.top"),sQuery(id+"F21.wireOp",EDGE,"E169.left"),sQuery(id+"F21.wireOp",EDGE,"E169.right"),sQuery(id+"F21.wireOp",EDGE,"E170"),sQuery(id+"F21.wireOp",EDGE,"E171.bottom"),sQuery(id+"F21.wireOp",EDGE,"E171.top"),sQuery(id+"F21.wireOp",EDGE,"E171.left"),sQuery(id+"F21.wireOp",EDGE,"E171.right"),sQuery(id+"F21.wireOp",EDGE,"E172"),sQuery(id+"F21.wireOp",EDGE,"E173"),sQuery(id+"F21.wireOp",EDGE,"E174"),sQuery(id+"F21.wireOp",EDGE,"E175"),sQuery(id+"F21.wireOp",EDGE,"E179"),sQuery(id+"F21.wireOp",EDGE,"E180.trimOffspring"),sQuery(id+"F21.wireOp",EDGE,"E181.trimOffspring"),sQuery(id+"F21.wireOp",EDGE,"E186"),sQuery(id+"F21.wireOp",EDGE,"E187"),sQuery(id+"F21.wireOp",EDGE,"E188.trimOffspring"),sQuery(id+"F21.wireOp",EDGE,"E189.trimOffspring"),sQuery(id+"F21.wireOp",EDGE,"E203"),sQuery(id+"F21.wireOp",EDGE,"E204"),sQuery(id+"F21.wireOp",EDGE,"E205"),sQuery(id+"F21.wireOp",EDGE,"E206"),sQuery(id+"F21.wireOp",EDGE,"E210.trimOffspring"),sQuery(id+"F21.wireOp",EDGE,"E211.trimOffspring"),sQuery(id+"F21.wireOp",EDGE,"E212.trimOffspring"),sQuery(id+"F21.wireOp",EDGE,"E213.trimOffspring"),sQuery(id+"F21.wireOp",EDGE,"E214"),sQuery(id+"F21.wireOp",EDGE,"E215"),sQuery(id+"F21.wireOp",EDGE,"E216"),sQuery(id+"F21.wireOp",EDGE,"E217")])],"isStart":false}),makeQuery(id+"F22.opExtrude","CAP_FACE",FACE,{"disambiguationData":[OSD([sQuery(id+"F21.wireOp",EDGE,"E202"),sQuery(id+"F21.wireOp",EDGE,"E207"),sQuery(id+"F21.wireOp",EDGE,"E208.trimOffspring"),sQuery(id+"F21.wireOp",EDGE,"E209.trimOffspring")])],"isStart":false}),makeQuery(id+"F24.opExtrude","CAP_FACE",FACE,{"disambiguationData":[OSD([sQuery(id+"F23.wireOp",EDGE,"E218.bottom"),sQuery(id+"F23.wireOp",EDGE,"E218.top"),sQuery(id+"F23.wireOp",EDGE,"E218.right"),sQuery(id+"F23.wireOp",EDGE,"E221.trimOffspring"),sQuery(id+"F23.wireOp",EDGE,"E223"),sQuery(id+"F23.wireOp",EDGE,"E224"),sQuery(id+"F23.wireOp",EDGE,"E225"),sQuery(id+"F23.wireOp",EDGE,"E227"),sQuery(id+"F23.wireOp",EDGE,"E228.bottom"),sQuery(id+"F23.wireOp",EDGE,"E228.top"),sQuery(id+"F23.wireOp",EDGE,"E228.left"),sQuery(id+"F23.wireOp",EDGE,"E228.right"),sQuery(id+"F23.wireOp",EDGE,"E229.bottom"),sQuery(id+"F23.wireOp",EDGE,"E229.top"),sQuery(id+"F23.wireOp",EDGE,"E229.left"),sQuery(id+"F23.wireOp",EDGE,"E229.right"),sQuery(id+"F23.wireOp",EDGE,"E230.bottom"),sQuery(id+"F23.wireOp",EDGE,"E230.top"),sQuery(id+"F23.wireOp",EDGE,"E230.left"),sQuery(id+"F23.wireOp",EDGE,"E230.right"),sQuery(id+"F23.wireOp",EDGE,"E231"),sQuery(id+"F23.wireOp",EDGE,"E232.bottom"),sQuery(id+"F23.wireOp",EDGE,"E232.top"),sQuery(id+"F23.wireOp",EDGE,"E232.left"),sQuery(id+"F23.wireOp",EDGE,"E232.right"),sQuery(id+"F23.wireOp",EDGE,"E233"),sQuery(id+"F23.wireOp",EDGE,"E234"),sQuery(id+"F23.wireOp",EDGE,"E235"),sQuery(id+"F23.wireOp",EDGE,"E236"),sQuery(id+"F23.wireOp",EDGE,"E241.trimOffspring"),sQuery(id+"F23.wireOp",EDGE,"E242.trimOffspring"),sQuery(id+"F23.wireOp",EDGE,"E249.trimOffspring"),sQuery(id+"F23.wireOp",EDGE,"E250.trimOffspring"),sQuery(id+"F23.wireOp",EDGE,"E269.trimOffspring"),sQuery(id+"F23.wireOp",EDGE,"E270.trimOffspring"),sQuery(id+"F23.wireOp",EDGE,"E271.trimOffspring"),sQuery(id+"F23.wireOp",EDGE,"E272.trimOffspring"),sQuery(id+"F23.wireOp",EDGE,"E273.trimOffspring"),sQuery(id+"F23.wireOp",EDGE,"E274.trimOffspring"),sQuery(id+"F23.wireOp",EDGE,"E275"),sQuery(id+"F23.wireOp",EDGE,"E276"),sQuery(id+"F23.wireOp",EDGE,"E277"),sQuery(id+"F23.wireOp",EDGE,"E279"),sQuery(id+"F23.wireOp",EDGE,"E280"),sQuery(id+"F23.wireOp",EDGE,"E281"),sQuery(id+"F23.wireOp",EDGE,"E282"),sQuery(id+"F23.wireOp",EDGE,"E283"),sQuery(id+"F23.wireOp",EDGE,"E284"),sQuery(id+"F23.wireOp",EDGE,"E285"),sQuery(id+"F23.wireOp",EDGE,"E286"),sQuery(id+"F23.wireOp",EDGE,"E287"),sQuery(id+"F23.wireOp",EDGE,"E288")])],"isStart":true})]});
            var sketch = newSketch(context, id + "F25", { "sketchPlane" : qUnion([Q0])});
            skLineSegment(sketch, "E289.bottom", {"start": v(0, 6000) * mm, "end": v(10000, 6000) * mm});
            skLineSegment(sketch, "E289.top", {"start": v(0, 0) * mm, "end": v(10000, 0) * mm});
            skLineSegment(sketch, "E289.left", {"start": v(0, 6000) * mm, "end": v(0, 0) * mm});
            skLineSegment(sketch, "E289.right", {"start": v(10000, 6000) * mm, "end": v(10000, 0) * mm});
            skSolve(sketch);
        }
        {
            var Q0;
            Q0 = qSketchRegion(id + "F25", true);
            extrude(context, id + "F26", {"entities" : qUnion([Q0]), "operationType" : NewBodyOperationType.ADD, "depth" : 25 * mm, "offsetDistance" : 25 * mm});
        }
    });
